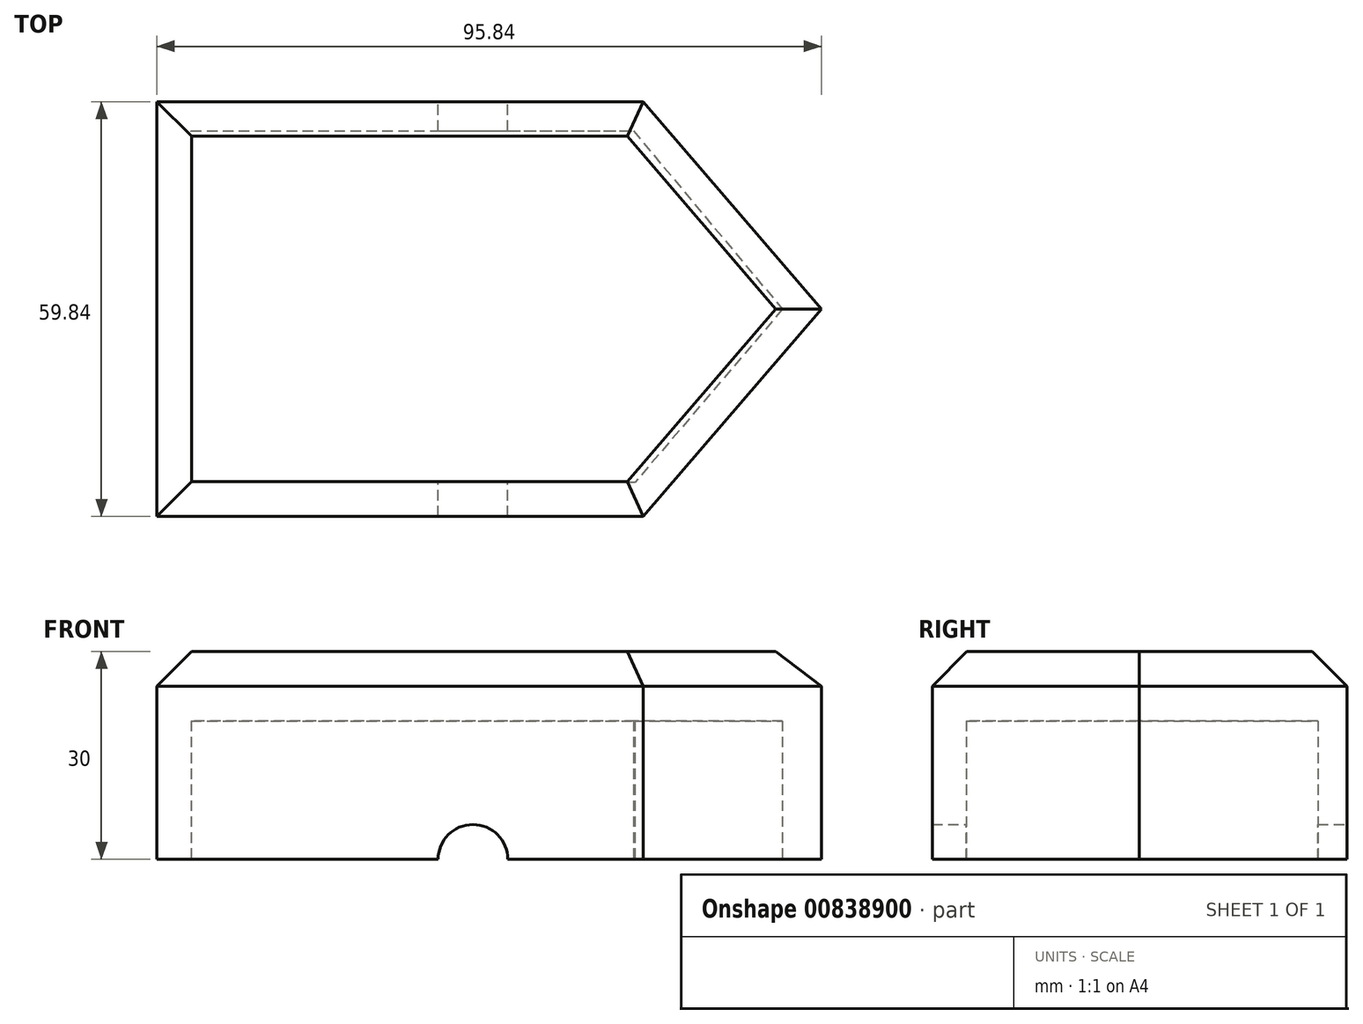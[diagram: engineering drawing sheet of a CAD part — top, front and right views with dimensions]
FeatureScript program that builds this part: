
annotation { "Feature Type Name" : "Feature", "Feature Type Description" : "" }
export const myFeature = defineFeature(function(context is Context, id is Id, definition is map)
    precondition{}
    {
        {
            var Q0;
            Q0=qCreatedBy(makeId("Top.planeOp"),FACE);
            var sketch = newSketch(context, id + "F0", { "sketchPlane" : qUnion([Q0])});
            skLineSegment(sketch, "E0", {"start": v(-55.03, 0) * mm, "end": v(-55.03, 29.96) * mm});
            skLineSegment(sketch, "E1", {"start": v(-55.03, 0) * mm, "end": v(-55.03, -29.88) * mm});
            skLineSegment(sketch, "E2", {"start": v(-55.03, 29.96) * mm, "end": v(15.1, 29.96) * mm});
            skLineSegment(sketch, "E3", {"start": v(-55.03, -29.88) * mm, "end": v(15.1, -29.88) * mm});
            skLineSegment(sketch, "E4", {"start": v(15.1, 29.96) * mm, "end": v(40.81, 0) * mm});
            skLineSegment(sketch, "E5", {"start": v(40.81, 0) * mm, "end": v(15.1, -29.88) * mm});
            skSolve(sketch);
        }
        {
            var Q0;
            Q0=makeQuery(id+"F0.imprint","IMPRINT",FACE,{"disambiguationData":[TD([[makeQuery(id+"F0.imprint","IMPRINT",EDGE,{"derivedFrom":sQuery(id+"F0.wireOp",EDGE,"E0")}),-1.0]])]});
            extrude(context, id + "F1", {"entities" : qUnion([Q0]), "depth" : 30 * mm, "offsetDistance" : 25 * mm});
        }
        {
            var Q0;
            Q0=makeQuery(id+"F1.opExtrude","CAP_FACE",FACE,{"disambiguationData":[OSD([sQuery(id+"F0.wireOp",EDGE,"E0"),sQuery(id+"F0.wireOp",EDGE,"E1"),sQuery(id+"F0.wireOp",EDGE,"E2"),sQuery(id+"F0.wireOp",EDGE,"E3"),sQuery(id+"F0.wireOp",EDGE,"E4"),sQuery(id+"F0.wireOp",EDGE,"E5")])],"isStart":true});
            var sketch = newSketch(context, id + "F2", { "sketchPlane" : qUnion([Q0])});
            skLineSegment(sketch, "E6", {"start": v(13.93, 24.97) * mm, "end": v(-50.12, 24.97) * mm});
            skLineSegment(sketch, "E7", {"start": v(-50.12, 24.97) * mm, "end": v(-50.12, -25.75) * mm});
            skLineSegment(sketch, "E8", {"start": v(-50.12, -25.75) * mm, "end": v(13.7, -25.75) * mm});
            skLineSegment(sketch, "E9", {"start": v(13.7, -25.75) * mm, "end": v(35.2, 0) * mm});
            skLineSegment(sketch, "E10", {"start": v(35.2, 0) * mm, "end": v(13.93, 24.97) * mm});
            skSolve(sketch);
        }
        {
            var Q0;
            Q0=makeQuery(id+"F2.imprint","IMPRINT",FACE,{"disambiguationData":[TD([[makeQuery(id+"F2.imprint","IMPRINT",EDGE,{"derivedFrom":sQuery(id+"F2.wireOp",EDGE,"E6")}),1.0]])]});
            extrude(context, id + "F3", {"entities" : qUnion([Q0]), "operationType" : NewBodyOperationType.REMOVE, "oppositeDirection" : true, "depth" : 20 * mm, "offsetDistance" : 25 * mm});
        }
        {
            var Q0;
            Q0=makeQuery(id+"F1.opExtrude","CAP_EDGE",EDGE,{"disambiguationData":[OSD([sQuery(id+"F0.wireOp",EDGE,"E5")])],"isStart":false});
            var Q1;
            Q1=makeQuery(id+"F1.opExtrude","CAP_EDGE",EDGE,{"disambiguationData":[OSD([sQuery(id+"F0.wireOp",EDGE,"E4")])],"isStart":false});
            var Q2;
            Q2=makeQuery(id+"F1.opExtrude","CAP_EDGE",EDGE,{"disambiguationData":[OSD([sQuery(id+"F0.wireOp",EDGE,"E2")])],"isStart":false});
            var Q3;
            Q3=makeQuery(id+"F1.opExtrude","CAP_EDGE",EDGE,{"disambiguationData":[OSD([sQuery(id+"F0.wireOp",EDGE,"E3")])],"isStart":false});
            var Q4;
            Q4=makeQuery(id+"F1.opExtrude","CAP_EDGE",EDGE,{"disambiguationData":[OSD([sQuery(id+"F0.wireOp",EDGE,"E0"),sQuery(id+"F0.wireOp",EDGE,"E1")])],"isStart":false});
            chamfer(context, id + "F4", {"entities" : qUnion([Q0, Q1, Q2, Q3, Q4]), "width" : 5 * mm, "tangentPropagation" : true});
        }
        {
            var Q0;
            Q0=makeQuery(id+"F1.opExtrude","SWEPT_FACE",FACE,{"disambiguationData":[OSD([sQuery(id+"F0.wireOp",EDGE,"E2")])]});
            var sketch = newSketch(context, id + "F5", { "sketchPlane" : qUnion([Q0])});
            skCircle(sketch, "E11", {"center": v(9.45, 0) * mm, "radius": 5.03 * mm});
            skSolve(sketch);
        }
        {
            var Q0;
            {var subQ0=sQuery(id+"F5.wireOp",EDGE,"E11");var subQ1=makeQuery(id+"F1.opExtrude","CAP_EDGE",EDGE,{"disambiguationData":[OSD([sQuery(id+"F0.wireOp",EDGE,"E2")])],"isStart":true});var subQ2=makeQuery(id+"F5.imprint","INTERSECT",VERTEX,{"disambiguationData":[OD(0.0)],"derivedFrom":[subQ1,subQ0]});Q0=makeQuery(id+"F5.imprint","IMPRINT",FACE,{"disambiguationData":[TD([[makeQuery(id+"F5.imprint","IMPRINT",EDGE,{"disambiguationData":[TD([[subQ2,-1.0]])],"derivedFrom":subQ0}),1.0]])]});}
            extrude(context, id + "F6", {"entities" : qUnion([Q0]), "operationType" : NewBodyOperationType.REMOVE, "oppositeDirection" : true, "depth" : 100 * mm, "offsetDistance" : 25 * mm});
        }
    });
